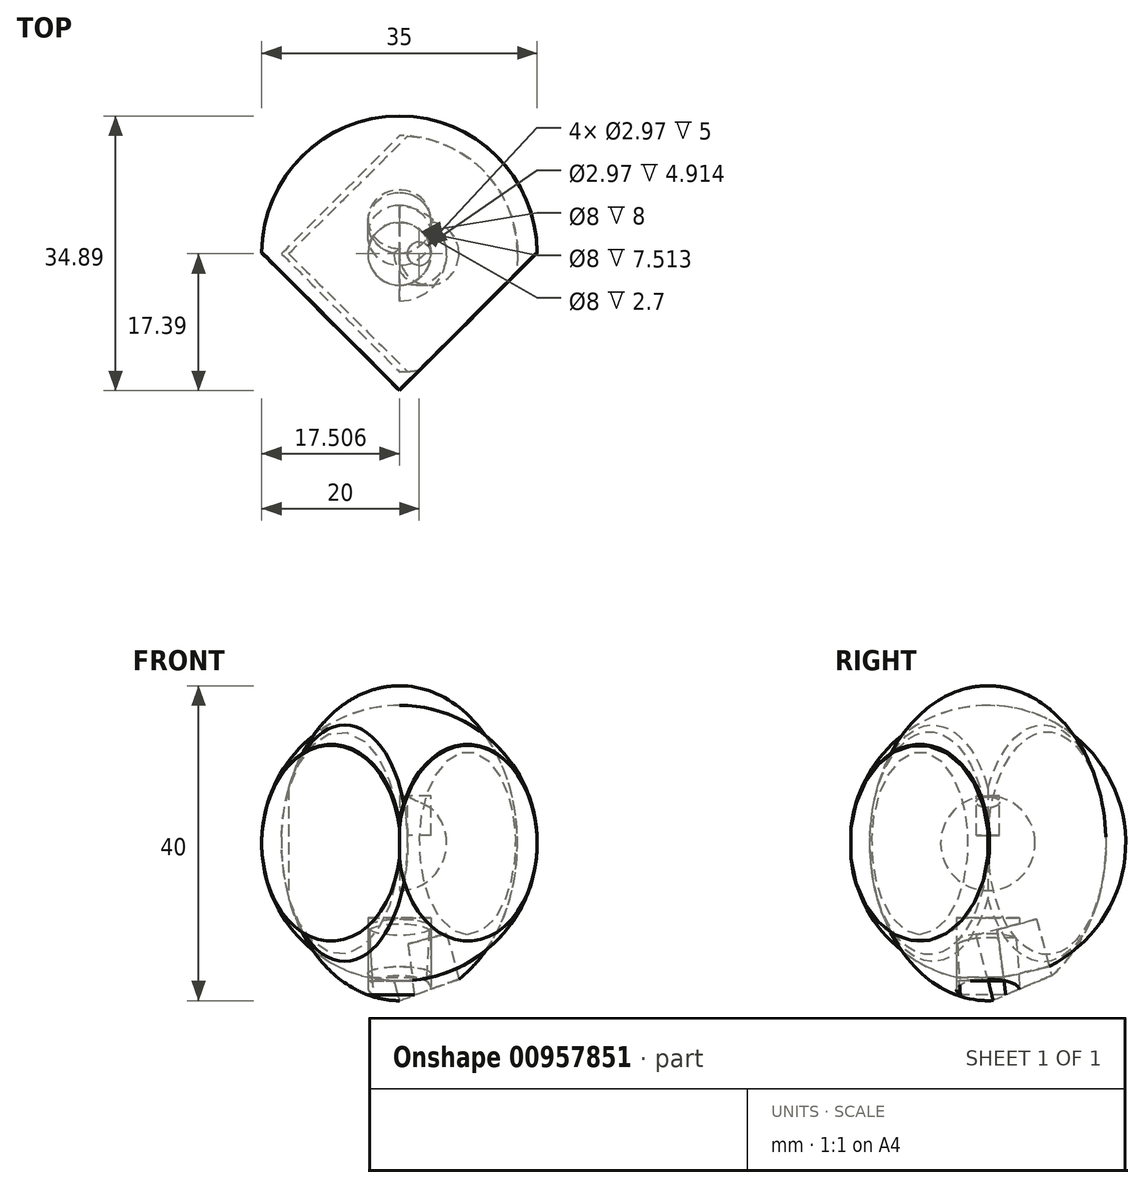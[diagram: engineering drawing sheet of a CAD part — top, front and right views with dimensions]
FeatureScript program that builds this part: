
annotation { "Feature Type Name" : "Feature", "Feature Type Description" : "" }
export const myFeature = defineFeature(function(context is Context, id is Id, definition is map)
    precondition{}
    {
        {
            var Q0;
            Q0=qCreatedBy(makeId("Front.planeOp"),FACE);
            var sketch = newSketch(context, id + "F0", { "sketchPlane" : qUnion([Q0])});
            skEllipticalArc(sketch, "E0", {});
            skLineSegment(sketch, "E1", {"start": v(0, 27.24) * mm, "end": v(0, -24.21) * mm, "construction": true});
            skPoint(sketch, "E1.endSnap0", {"position": v(0, -20) * mm});
            skLineSegment(sketch, "E2", {"start": v(-16.84, 0) * mm, "end": v(18.26, 0) * mm, "construction": true});
            skLineSegment(sketch, "E3", {"start": v(0, 20) * mm, "end": v(0, -20) * mm});
            const initialGuessF0  = {"E0": [0, 0, 0, -1, 0.02, 0.015, 0, 3.141592653589793]};
            skSetInitialGuess(sketch, initialGuessF0);
            skSolve(sketch);
        }
        {
            var Q0;
            Q0 = qSketchRegion(id + "F0", true);
            var Q1;
            Q1=sQuery(id+"F0.wireOp",EDGE,"E1");
            revolve(context, id + "F1", {"surfaceOperationType" : NewSurfaceOperationType.NEW, "entities" : qUnion([Q0]), "axis" : qUnion([Q1]), "revolveType" : RevolveType.FULL});
        }
        {
            var Q0;
            Q0=qCreatedBy(makeId("Top.planeOp"),FACE);
            var sketch = newSketch(context, id + "F2", { "sketchPlane" : qUnion([Q0])});
            skLineSegment(sketch, "E4", {"start": v(23.65, 0) * mm, "end": v(-93.06, 0) * mm, "construction": true});
            skLineSegment(sketch, "E5", {"start": v(-15, -40.43) * mm, "end": v(-15, 47.08) * mm, "construction": true});
            skLineSegment(sketch, "E6", {"start": v(1.09, -16.13) * mm, "end": v(1.09, 16.61) * mm, "construction": true});
            skLineSegment(sketch, "E7", {"start": v(14.94, 0) * mm, "end": v(14.94, 17.37) * mm, "construction": true});
            skLineSegment(sketch, "E8", {"start": v(-14.06, 16.82) * mm, "end": v(-14.06, -16.29) * mm, "construction": true});
            skLineSegment(sketch, "E9", {"start": v(1.09, -15.03) * mm, "end": v(-14.06, 0) * mm});
            skLineSegment(sketch, "E10", {"start": v(-14.06, 0) * mm, "end": v(1.09, 14.97) * mm});
            skLineSegment(sketch, "E11", {"start": v(1.09, 14.97) * mm, "end": v(1.09, 17.46) * mm});
            skLineSegment(sketch, "E12", {"start": v(1.09, 17.46) * mm, "end": v(-20.62, 17.98) * mm});
            skLineSegment(sketch, "E13", {"start": v(-20.62, 17.98) * mm, "end": v(-19.67, -17.44) * mm});
            skLineSegment(sketch, "E14", {"start": v(-19.67, -17.44) * mm, "end": v(1.09, -18.07) * mm});
            skLineSegment(sketch, "E15", {"start": v(1.09, -18.07) * mm, "end": v(1.09, -15.03) * mm});
            skSolve(sketch);
        }
        {
            var Q0;
            Q0 = qSketchRegion(id + "F2", true);
            extrude(context, id + "F3", {"entities" : qUnion([Q0]), "operationType" : NewBodyOperationType.REMOVE, "endBound" : BoundingType.THROUGH_ALL, "depth" : 25 * mm, "offsetDistance" : 25 * mm, "hasSecondDirection" : true, "secondDirectionOppositeDirection" : true, "secondDirectionDepth" : 25 * mm});
        }
        {
            var Q0;
            Q0=qCreatedBy(makeId("Top.planeOp"),FACE);
            cPlane(context, id + "F4", {"entities" : qUnion([Q0]), "cplaneType" : CPlaneType.OFFSET, "offset" : 20.2 * mm, "oppositeDirection" : true, "width" : 150 * mm, "height" : 150 * mm});
        }
        {
            var Q0;
            Q0=qCreatedBy(id+"F4.planeOp",FACE);
            var sketch = newSketch(context, id + "F5", { "sketchPlane" : qUnion([Q0])});
            skCircle(sketch, "E16", {"center": v(0, 0) * mm, "radius": 4 * mm});
            skSolve(sketch);
        }
        {
            var Q0;
            Q0 = qSketchRegion(id + "F5", true);
            extrude(context, id + "F6", {"entities" : qUnion([Q0]), "operationType" : NewBodyOperationType.REMOVE, "depth" : 8 * mm, "offsetDistance" : 25 * mm});
        }
        {
            var Q0;
            Q0=qCreatedBy(makeId("Front.planeOp"),FACE);
            var sketch = newSketch(context, id + "F7", { "sketchPlane" : qUnion([Q0])});
            skEllipticalArc(sketch, "E17", {});
            skLineSegment(sketch, "E18", {"start": v(0, 20) * mm, "end": v(0, -20) * mm});
            const initialGuessF7  = {"E17": [0, 0, 0, 1, 0.02, 0.015, 3.141592653589793, 0]};
            skSetInitialGuess(sketch, initialGuessF7);
            skSolve(sketch);
        }
        {
            var Q0;
            Q0 = qSketchRegion(id + "F7", true);
            var Q1;
            Q1=sQuery(id+"F7.wireOp",EDGE,"E18");
            revolve(context, id + "F8", {"surfaceOperationType" : NewSurfaceOperationType.NEW, "entities" : qUnion([Q0]), "axis" : qUnion([Q1]), "revolveType" : RevolveType.FULL});
        }
        {
            var Q0;
            Q0=qCreatedBy(makeId("Top.planeOp"),FACE);
            var sketch = newSketch(context, id + "F9", { "sketchPlane" : qUnion([Q0])});
            skLineSegment(sketch, "E19", {"start": v(23.65, 0) * mm, "end": v(-93.06, 0) * mm, "construction": true});
            skLineSegment(sketch, "E20", {"start": v(-14.99, -40.45) * mm, "end": v(-14.99, 47.06) * mm, "construction": true});
            skLineSegment(sketch, "E21", {"start": v(1.09, -16.15) * mm, "end": v(1.09, 16.6) * mm, "construction": true});
            skLineSegment(sketch, "E22", {"start": v(14.01, 0) * mm, "end": v(14.01, 17.36) * mm, "construction": true});
            skLineSegment(sketch, "E23", {"start": v(-14.99, 16.8) * mm, "end": v(-14.99, -16.3) * mm, "construction": true});
            skLineSegment(sketch, "E24", {"start": v(2.1, -17.09) * mm, "end": v(-14.99, 0) * mm});
            skLineSegment(sketch, "E25", {"start": v(-14.99, 0) * mm, "end": v(3.71, 18.7) * mm});
            skLineSegment(sketch, "E26", {"start": v(-20.62, 17.96) * mm, "end": v(-19.67, -17.46) * mm});
            skLineSegment(sketch, "E27", {"start": v(3.71, 18.7) * mm, "end": v(-20.62, 17.96) * mm});
            skLineSegment(sketch, "E28", {"start": v(2.1, -17.09) * mm, "end": v(-19.67, -17.46) * mm});
            skSolve(sketch);
        }
        {
            var Q0;
            Q0 = qSketchRegion(id + "F9", true);
            extrude(context, id + "F10", {"entities" : qUnion([Q0]), "operationType" : NewBodyOperationType.REMOVE, "endBound" : BoundingType.THROUGH_ALL, "depth" : 25 * mm, "offsetDistance" : 25 * mm, "hasSecondDirection" : true, "secondDirectionOppositeDirection" : true, "secondDirectionDepth" : 25 * mm});
        }
        {
            var Q0;
            Q0=qCreatedBy(makeId("Front.planeOp"),FACE);
            var sketch = newSketch(context, id + "F11", { "sketchPlane" : qUnion([Q0])});
            skLineSegment(sketch, "E29", {"start": v(-11.22, -28.3) * mm, "end": v(35.1, -15.88) * mm, "construction": true});
            skLineSegment(sketch, "E30", {"start": v(-11.22, -28.3) * mm, "end": v(-11.22, 29.1) * mm, "construction": true});
            skSolve(sketch);
        }
        {
            var Q0;
            Q0=sQuery(id+"F11.wireOp",EDGE,"E29");
            var Q1;
            Q1=qCreatedBy(id+"F4.planeOp",FACE);
            cPlane(context, id + "F12", {"entities" : qUnion([Q0, Q1]), "cplaneType" : CPlaneType.LINE_ANGLE, "offset" : 25 * mm, "angle" : 0 * degree, "width" : 150 * mm, "height" : 150 * mm});
        }
        {
            var Q0;
            Q0=qCreatedBy(id+"F12.planeOp",FACE);
            var sketch = newSketch(context, id + "F13", { "sketchPlane" : qUnion([Q0])});
            skLineSegment(sketch, "E31", {"start": v(-16.4, 0) * mm, "end": v(26.02, 0) * mm, "construction": true});
            skCircle(sketch, "E32", {"center": v(-1.18, 0) * mm, "radius": 4 * mm});
            skSolve(sketch);
        }
        {
            var Q0;
            Q0 = qSketchRegion(id + "F13", true);
            extrude(context, id + "F14", {"entities" : qUnion([Q0]), "operationType" : NewBodyOperationType.REMOVE, "oppositeDirection" : true, "depth" : 11.78 * mm, "offsetDistance" : 25 * mm});
        }
        {
            var Q0;
            Q0=qCreatedBy(makeId("Front.planeOp"),FACE);
            var sketch = newSketch(context, id + "F15", { "sketchPlane" : qUnion([Q0])});
            skArc(sketch, "E33", {"start": v(0, -17.48) * mm, "mid": v(17.5, 0.02) * mm, "end": v(0, 17.52) * mm});
            skLineSegment(sketch, "E34", {"start": v(0, -17.48) * mm, "end": v(0, 17.52) * mm});
            skSolve(sketch);
        }
        {
            var Q0;
            Q0 = qSketchRegion(id + "F15", true);
            var Q1;
            Q1=sQuery(id+"F15.wireOp",EDGE,"E34");
            revolve(context, id + "F16", {"surfaceOperationType" : NewSurfaceOperationType.NEW, "entities" : qUnion([Q0]), "axis" : qUnion([Q1]), "revolveType" : RevolveType.FULL});
        }
        {
            var Q0;
            Q0=qCreatedBy(makeId("Top.planeOp"),FACE);
            var sketch = newSketch(context, id + "F17", { "sketchPlane" : qUnion([Q0])});
            skCircle(sketch, "E35", {"center": v(0, -17.29) * mm, "radius": 25 * mm, "construction": true});
            skLineSegment(sketch, "E36", {"start": v(0, -17.29) * mm, "end": v(19.99, 2.7) * mm});
            skLineSegment(sketch, "E37", {"start": v(0, -17.29) * mm, "end": v(-21.62, 4.33) * mm});
            skLineSegment(sketch, "E38", {"start": v(15.28, -17.29) * mm, "end": v(-17.47, -17.29) * mm, "construction": true});
            skLineSegment(sketch, "E39", {"start": v(-21.62, 4.33) * mm, "end": v(-21.62, -23.65) * mm});
            skLineSegment(sketch, "E40", {"start": v(-21.62, -23.65) * mm, "end": v(21.96, -24.4) * mm});
            skLineSegment(sketch, "E41", {"start": v(21.96, -24.4) * mm, "end": v(19.99, 2.7) * mm});
            skSolve(sketch);
        }
        {
            var Q0;
            Q0 = qSketchRegion(id + "F17", true);
            extrude(context, id + "F18", {"entities" : qUnion([Q0]), "operationType" : NewBodyOperationType.REMOVE, "endBound" : BoundingType.THROUGH_ALL, "oppositeDirection" : true, "depth" : 25 * mm, "offsetDistance" : 25 * mm, "hasSecondDirection" : true, "secondDirectionOppositeDirection" : false, "secondDirectionDepth" : 25 * mm});
        }
        {
            var Q0;
            Q0=qCreatedBy(makeId("Top.planeOp"),FACE);
            cPlane(context, id + "F19", {"entities" : qUnion([Q0]), "cplaneType" : CPlaneType.OFFSET, "offset" : 17.5 * mm, "oppositeDirection" : true, "width" : 150 * mm, "height" : 150 * mm});
        }
        {
            var Q0;
            Q0=qCreatedBy(id+"F19.planeOp",FACE);
            var sketch = newSketch(context, id + "F20", { "sketchPlane" : qUnion([Q0])});
            skCircle(sketch, "E42", {"center": v(0, 0) * mm, "radius": 4 * mm});
            skSolve(sketch);
        }
        {
            var Q0;
            Q0 = qSketchRegion(id + "F20", true);
            extrude(context, id + "F21", {"entities" : qUnion([Q0]), "operationType" : NewBodyOperationType.REMOVE, "depth" : 8 * mm, "offsetDistance" : 25 * mm});
        }
        {
            var Q0;
            Q0=qCreatedBy(makeId("Front.planeOp"),FACE);
            var sketch = newSketch(context, id + "F22", { "sketchPlane" : qUnion([Q0])});
            skArc(sketch, "E43", {"start": v(0, -17.5) * mm, "mid": v(17.5, 0) * mm, "end": v(0, 17.5) * mm});
            skLineSegment(sketch, "E44", {"start": v(0, -17.5) * mm, "end": v(0, 17.5) * mm});
            skSolve(sketch);
        }
        {
            var Q0;
            Q0 = qSketchRegion(id + "F22", true);
            var Q1;
            Q1=sQuery(id+"F22.wireOp",EDGE,"E44");
            revolve(context, id + "F23", {"surfaceOperationType" : NewSurfaceOperationType.NEW, "entities" : qUnion([Q0]), "axis" : qUnion([Q1]), "revolveType" : RevolveType.FULL});
        }
        {
            var Q0;
            Q0=qCreatedBy(makeId("Top.planeOp"),FACE);
            var sketch = newSketch(context, id + "F24", { "sketchPlane" : qUnion([Q0])});
            skCircle(sketch, "E45", {"center": v(0, -17.4) * mm, "radius": 25 * mm, "construction": true});
            skLineSegment(sketch, "E46", {"start": v(0, -17.4) * mm, "end": v(22.6, 5.2) * mm});
            skLineSegment(sketch, "E47", {"start": v(0, -17.4) * mm, "end": v(-21.62, 4.23) * mm});
            skLineSegment(sketch, "E48", {"start": v(15.28, -17.4) * mm, "end": v(-17.47, -17.4) * mm, "construction": true});
            skLineSegment(sketch, "E49", {"start": v(-21.62, 4.23) * mm, "end": v(-21.62, -25.09) * mm});
            skLineSegment(sketch, "E50", {"start": v(-21.62, -25.09) * mm, "end": v(21.62, -25.84) * mm});
            skLineSegment(sketch, "E51", {"start": v(22.6, 5.2) * mm, "end": v(21.62, -25.84) * mm});
            skPoint(sketch, "E52", {"position": v(0, -25.47) * mm});
            skSolve(sketch);
        }
        {
            var Q0;
            Q0 = qSketchRegion(id + "F24", true);
            extrude(context, id + "F25", {"entities" : qUnion([Q0]), "operationType" : NewBodyOperationType.REMOVE, "endBound" : BoundingType.THROUGH_ALL, "oppositeDirection" : true, "depth" : 25 * mm, "offsetDistance" : 25 * mm, "hasSecondDirection" : true, "secondDirectionOppositeDirection" : false, "secondDirectionDepth" : 25 * mm});
        }
        {
            var Q0;
            Q0=qCreatedBy(makeId("Front.planeOp"),FACE);
            var sketch = newSketch(context, id + "F26", { "sketchPlane" : qUnion([Q0])});
            skLineSegment(sketch, "E53", {"start": v(-27.38, -21.33) * mm, "end": v(28.68, -21.33) * mm, "construction": true});
            skSolve(sketch);
        }
        {
            var Q0;
            Q0=qCreatedBy(id+"F19.planeOp",FACE);
            var Q1;
            Q1=sQuery(id+"F26.wireOp",EDGE,"E53");
            cPlane(context, id + "F27", {"entities" : qUnion([Q0, Q1]), "cplaneType" : CPlaneType.LINE_ANGLE, "offset" : 25 * mm, "angle" : 15 * degree, "width" : 150 * mm, "height" : 150 * mm});
        }
        {
            var Q0;
            Q0=qCreatedBy(id+"F27.planeOp",FACE);
            var sketch = newSketch(context, id + "F28", { "sketchPlane" : qUnion([Q0])});
            skCircle(sketch, "E54", {"center": v(0, 0.52) * mm, "radius": 4 * mm});
            skSolve(sketch);
        }
        {
            var Q0;
            Q0 = qSketchRegion(id + "F28", true);
            extrude(context, id + "F29", {"entities" : qUnion([Q0]), "operationType" : NewBodyOperationType.REMOVE, "oppositeDirection" : true, "depth" : (13.9 - 4.2) * mm, "offsetDistance" : 25 * mm});
        }
        {
            var Q0;
            Q0=qCreatedBy(makeId("Front.planeOp"),FACE);
            var sketch = newSketch(context, id + "F30", { "sketchPlane" : qUnion([Q0])});
            skArc(sketch, "E55", {"start": v(6, 0) * mm, "mid": v(4.24, 4.24) * mm, "end": v(0, 6) * mm});
            skLineSegment(sketch, "E56", {"start": v(0, 6) * mm, "end": v(0, 0) * mm});
            skLineSegment(sketch, "E57", {"start": v(0, 0) * mm, "end": v(6, 0) * mm});
            skSolve(sketch);
        }
        {
            var Q0;
            Q0 = qSketchRegion(id + "F30", true);
            var Q1;
            Q1=sQuery(id+"F30.wireOp",EDGE,"E57");
            revolve(context, id + "F31", {"surfaceOperationType" : NewSurfaceOperationType.NEW, "entities" : qUnion([Q0]), "axis" : qUnion([Q1]), "revolveType" : RevolveType.FULL});
        }
        {
            var Q0;
            Q0=qCreatedBy(makeId("Top.planeOp"),FACE);
            cPlane(context, id + "F32", {"entities" : qUnion([Q0]), "cplaneType" : CPlaneType.OFFSET, "offset" : 6 * mm, "width" : 150 * mm, "height" : 150 * mm});
        }
        {
            var Q0;
            Q0=qCreatedBy(id+"F32.planeOp",FACE);
            var sketch = newSketch(context, id + "F33", { "sketchPlane" : qUnion([Q0])});
            skCircle(sketch, "E58", {"center": v(2.5, 0) * mm, "radius": 1.49 * mm});
            skSolve(sketch);
        }
        {
            var Q0;
            Q0 = qSketchRegion(id + "F33", true);
            extrude(context, id + "F34", {"entities" : qUnion([Q0]), "operationType" : NewBodyOperationType.REMOVE, "oppositeDirection" : true, "depth" : 5 * mm, "offsetDistance" : 25 * mm});
        }
    });
